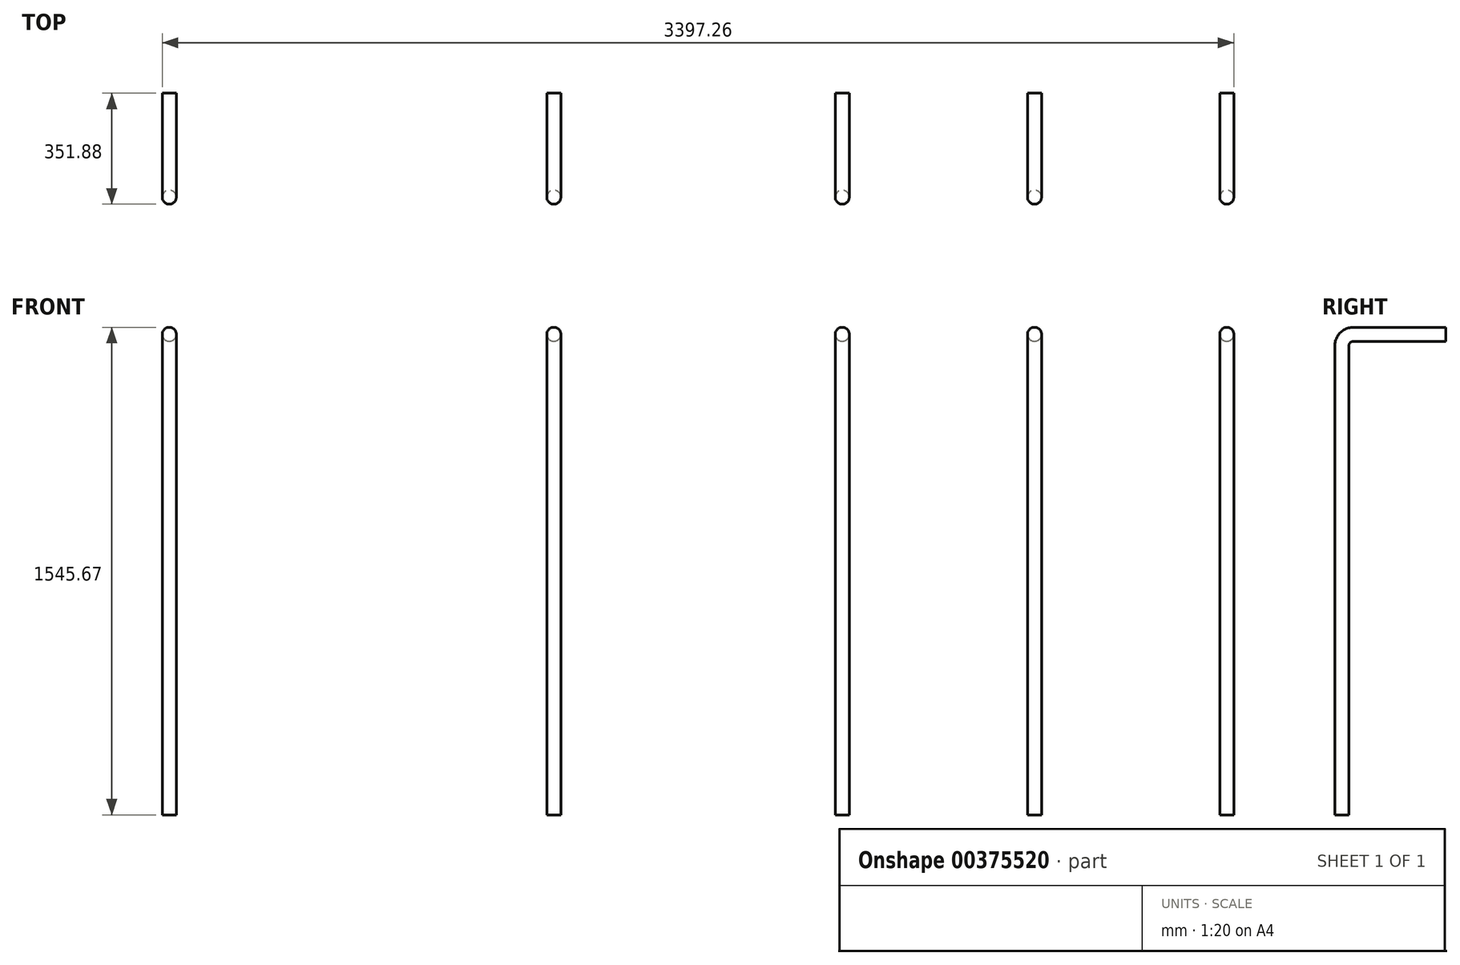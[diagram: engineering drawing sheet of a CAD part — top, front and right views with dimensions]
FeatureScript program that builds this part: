
annotation { "Feature Type Name" : "Feature", "Feature Type Description" : "" }
export const myFeature = defineFeature(function(context is Context, id is Id, definition is map)
    precondition{}
    {
        {
            var Q0;
            Q0=qCreatedBy(makeId("Top.planeOp"),FACE);
            cPlane(context, id + "F0", {"entities" : qUnion([Q0]), "cplaneType" : CPlaneType.OFFSET, "offset" : 381 * mm, "width" : 152.4 * mm, "height" : 152.4 * mm});
        }
        {
            var Q0;
            Q0=qCreatedBy(makeId("Top.planeOp"),FACE);
            cPlane(context, id + "F1", {"entities" : qUnion([Q0]), "cplaneType" : CPlaneType.OFFSET, "offset" : 685.8 * mm, "width" : 152.4 * mm, "height" : 152.4 * mm});
        }
        {
            var Q0;
            Q0=qCreatedBy(makeId("Top.planeOp"),FACE);
            cPlane(context, id + "F2", {"entities" : qUnion([Q0]), "cplaneType" : CPlaneType.OFFSET, "offset" : 1041.4 * mm, "width" : 152.4 * mm, "height" : 152.4 * mm});
        }
        {
            var Q0;
            Q0=qCreatedBy(makeId("Top.planeOp"),FACE);
            var sketch = newSketch(context, id + "F3", { "sketchPlane" : qUnion([Q0])});
            skLineSegment(sketch, "E0.bottom", {"start": v(-1727.2, 190.5) * mm, "end": v(1727.2, 190.5) * mm});
            skLineSegment(sketch, "E0.top", {"start": v(-1727.2, -190.5) * mm, "end": v(1727.2, -190.5) * mm});
            skLineSegment(sketch, "E0.left", {"start": v(-1727.2, 190.5) * mm, "end": v(-1727.2, -190.5) * mm});
            skLineSegment(sketch, "E0.right", {"start": v(1727.2, 190.5) * mm, "end": v(1727.2, -190.5) * mm});
            skPoint(sketch, "E0.middle", {"position": v(0, 0) * mm});
            skSolve(sketch);
        }
        {
            var Q0;
            Q0=qCreatedBy(id+"F1.planeOp",FACE);
            var sketch = newSketch(context, id + "F4", { "sketchPlane" : qUnion([Q0])});
            skLineSegment(sketch, "E1.0.0", {"start": v(-1727.2, 190.5) * mm, "end": v(-1727.2, -190.5) * mm});
            skLineSegment(sketch, "E1.0.1", {"start": v(-1727.2, -190.5) * mm, "end": v(1727.2, -190.5) * mm});
            skLineSegment(sketch, "E1.0.2", {"start": v(1727.2, -190.5) * mm, "end": v(1727.2, 190.5) * mm});
            skLineSegment(sketch, "E1.0.3", {"start": v(1727.2, 190.5) * mm, "end": v(-1727.2, 190.5) * mm});
            skSolve(sketch);
        }
        {
            var Q0;
            Q0=qCreatedBy(id+"F2.planeOp",FACE);
            var sketch = newSketch(context, id + "F5", { "sketchPlane" : qUnion([Q0])});
            skLineSegment(sketch, "E2.bottom", {"start": v(-406.4, -190.5) * mm, "end": v(-1727.2, -190.5) * mm});
            skLineSegment(sketch, "E2.top", {"start": v(-406.4, 190.5) * mm, "end": v(-1727.2, 190.5) * mm});
            skLineSegment(sketch, "E2.left", {"start": v(-406.4, -190.5) * mm, "end": v(-406.4, 190.5) * mm});
            skLineSegment(sketch, "E2.right", {"start": v(-1727.2, -190.5) * mm, "end": v(-1727.2, 190.5) * mm});
            skPoint(sketch, "E2.middle", {"position": v(-1066.8, 0) * mm});
            skLineSegment(sketch, "E3.bottom", {"start": v(1727.2, -190.5) * mm, "end": v(406.4, -190.5) * mm});
            skLineSegment(sketch, "E3.top", {"start": v(1727.2, 190.5) * mm, "end": v(406.4, 190.5) * mm});
            skLineSegment(sketch, "E3.left", {"start": v(1727.2, -190.5) * mm, "end": v(1727.2, 190.5) * mm});
            skLineSegment(sketch, "E3.right", {"start": v(406.4, -190.5) * mm, "end": v(406.4, 190.5) * mm});
            skPoint(sketch, "E3.middle", {"position": v(1066.8, 0) * mm});
            skSolve(sketch);
        }
        {
            var Q0;
            Q0=qCreatedBy(id+"F0.planeOp",FACE);
            var sketch = newSketch(context, id + "F6", { "sketchPlane" : qUnion([Q0])});
            skLineSegment(sketch, "E4.0.1", {"start": v(-406.4, 190.5) * mm, "end": v(-1727.2, 190.5) * mm});
            skLineSegment(sketch, "E4.0.2", {"start": v(-1727.2, 190.5) * mm, "end": v(-1727.2, -190.5) * mm});
            skLineSegment(sketch, "E4.0.3", {"start": v(-1727.2, -190.5) * mm, "end": v(-406.4, -190.5) * mm});
            skLineSegment(sketch, "E5.0.0", {"start": v(1727.2, -190.5) * mm, "end": v(1727.2, 190.5) * mm});
            skLineSegment(sketch, "E5.0.1", {"start": v(1727.2, 190.5) * mm, "end": v(406.4, 190.5) * mm});
            skLineSegment(sketch, "E5.0.2", {"start": v(406.4, 190.5) * mm, "end": v(406.4, -190.5) * mm});
            skLineSegment(sketch, "E5.0.3", {"start": v(406.4, -190.5) * mm, "end": v(1727.2, -190.5) * mm});
            skSolve(sketch);
        }
        {
            var Q0;
            Q0=qCreatedBy(makeId("Top.planeOp"),FACE);
            var sketch = newSketch(context, id + "F7", { "sketchPlane" : qUnion([Q0])});
            skCircle(sketch, "E6", {"center": v(-1676.4, -139.7) * mm, "radius": 22.23 * mm});
            skLineSegment(sketch, "E7", {"start": v(-1727.2, -139.7) * mm, "end": v(1727.2, -139.7) * mm, "construction": true});
            skLineSegment(sketch, "E8", {"start": v(-1676.4, -139.7) * mm, "end": v(-1676.4, -2659.55) * mm});
            skLineSegment(sketch, "E9", {"start": v(-457.2, -139.7) * mm, "end": v(-457.2, -2659.55) * mm});
            skLineSegment(sketch, "E10", {"start": v(457.2, -139.7) * mm, "end": v(457.2, -2659.55) * mm});
            skLineSegment(sketch, "E11", {"start": v(1066.8, -139.7) * mm, "end": v(1066.8, -2659.55) * mm});
            skLineSegment(sketch, "E12", {"start": v(1676.4, -139.7) * mm, "end": v(1676.4, -2659.55) * mm});
            skLineSegment(sketch, "E13", {"start": v(457.2, -139.7) * mm, "end": v(-457.2, -139.7) * mm, "construction": true});
            skPoint(sketch, "E14", {"position": v(0, -139.7) * mm});
            skCircle(sketch, "E15", {"center": v(-457.2, -139.7) * mm, "radius": 22.23 * mm});
            skCircle(sketch, "E16", {"center": v(457.2, -139.7) * mm, "radius": 22.23 * mm});
            skCircle(sketch, "E17", {"center": v(1066.8, -139.7) * mm, "radius": 22.23 * mm});
            skCircle(sketch, "E18", {"center": v(1676.4, -139.7) * mm, "radius": 22.23 * mm});
            skSolve(sketch);
        }
        {
            var Q0;
            Q0=qCreatedBy(makeId("Top.planeOp"),FACE);
            var sketch = newSketch(context, id + "F8", { "sketchPlane" : qUnion([Q0])});
            skSolve(sketch);
        }
        {
            var Q0;
            Q0=qCreatedBy(makeId("Right.planeOp"),FACE);
            var sketch = newSketch(context, id + "F9", { "sketchPlane" : qUnion([Q0])});
            skLineSegment(sketch, "E19", {"start": v(-140.25, 0) * mm, "end": v(-140.25, 1485.9) * mm});
            skLineSegment(sketch, "E20", {"start": v(-102.15, 1524) * mm, "end": v(189.95, 1524) * mm});
            skPoint(sketch, "E21.visualSharp", {"position": v(-140.25, 1524) * mm});
            skArc(sketch, "E21.filletArc", {"start": v(-102.15, 1524) * mm, "mid": v(-129.1, 1512.84) * mm, "end": v(-140.25, 1485.9) * mm});
            skSolve(sketch);
        }
        {
            var Q0;
            Q0=qCreatedBy(makeId("Right.planeOp"),FACE);
            var Q1;
            Q1=sQuery(id+"F7.wireOp",VERTEX,"E16.center");
            cPlane(context, id + "F10", {"entities" : qUnion([Q0, Q1]), "cplaneType" : CPlaneType.PLANE_POINT, "offset" : 25.4 * mm, "width" : 152.4 * mm, "height" : 152.4 * mm});
        }
        {
            var Q0;
            Q0=qCreatedBy(id+"F10.planeOp",FACE);
            var sketch = newSketch(context, id + "F11", { "sketchPlane" : qUnion([Q0])});
            skLineSegment(sketch, "E22.0", {"start": v(-140.25, 0) * mm, "end": v(-140.25, 1485.9) * mm});
            skArc(sketch, "E23.0", {"start": v(-102.15, 1524) * mm, "mid": v(-129.1, 1512.84) * mm, "end": v(-140.25, 1485.9) * mm});
            skLineSegment(sketch, "E24.0", {"start": v(-102.15, 1524) * mm, "end": v(189.95, 1524) * mm});
            skSolve(sketch);
        }
        {
            var Q0;
            Q0=qCreatedBy(makeId("Right.planeOp"),FACE);
            var Q1;
            Q1=sQuery(id+"F7.wireOp",VERTEX,"E15.center");
            cPlane(context, id + "F12", {"entities" : qUnion([Q0, Q1]), "cplaneType" : CPlaneType.PLANE_POINT, "offset" : 25.4 * mm, "width" : 152.4 * mm, "height" : 152.4 * mm});
        }
        {
            var Q0;
            Q0=qCreatedBy(makeId("Right.planeOp"),FACE);
            var Q1;
            Q1=sQuery(id+"F7.wireOp",VERTEX,"E17.center");
            cPlane(context, id + "F13", {"entities" : qUnion([Q0, Q1]), "cplaneType" : CPlaneType.PLANE_POINT, "offset" : 25.4 * mm, "width" : 152.4 * mm, "height" : 152.4 * mm});
        }
        {
            var Q0;
            Q0=qCreatedBy(makeId("Right.planeOp"),FACE);
            var Q1;
            Q1=sQuery(id+"F7.wireOp",VERTEX,"E18.center");
            cPlane(context, id + "F14", {"entities" : qUnion([Q0, Q1]), "cplaneType" : CPlaneType.PLANE_POINT, "offset" : 25.4 * mm, "width" : 152.4 * mm, "height" : 152.4 * mm});
        }
        {
            var Q0;
            Q0=qCreatedBy(makeId("Right.planeOp"),FACE);
            var Q1;
            Q1=sQuery(id+"F7.wireOp",VERTEX,"E8.end");
            cPlane(context, id + "F15", {"entities" : qUnion([Q0, Q1]), "cplaneType" : CPlaneType.PLANE_POINT, "offset" : 25.4 * mm, "width" : 152.4 * mm, "height" : 152.4 * mm});
        }
        {
            var Q0;
            Q0=qCreatedBy(id+"F12.planeOp",FACE);
            var sketch = newSketch(context, id + "F16", { "sketchPlane" : qUnion([Q0])});
            skLineSegment(sketch, "E25.0", {"start": v(-102.15, 1524) * mm, "end": v(189.95, 1524) * mm});
            skLineSegment(sketch, "E26.0", {"start": v(-140.25, 0) * mm, "end": v(-140.25, 1485.9) * mm});
            skPoint(sketch, "E27.0", {"position": v(-129.1, 1512.84) * mm});
            skArc(sketch, "E28.0", {"start": v(-102.15, 1524) * mm, "mid": v(-129.1, 1512.84) * mm, "end": v(-140.25, 1485.9) * mm});
            skSolve(sketch);
        }
        {
            var Q0;
            Q0=qCreatedBy(id+"F13.planeOp",FACE);
            var sketch = newSketch(context, id + "F17", { "sketchPlane" : qUnion([Q0])});
            skLineSegment(sketch, "E29.0", {"start": v(-102.15, 1524) * mm, "end": v(189.95, 1524) * mm});
            skArc(sketch, "E30.0", {"start": v(-102.15, 1524) * mm, "mid": v(-129.1, 1512.84) * mm, "end": v(-140.25, 1485.9) * mm});
            skLineSegment(sketch, "E31.0", {"start": v(-140.25, 0) * mm, "end": v(-140.25, 1485.9) * mm});
            skSolve(sketch);
        }
        {
            var Q0;
            Q0=qCreatedBy(id+"F15.planeOp",FACE);
            var sketch = newSketch(context, id + "F18", { "sketchPlane" : qUnion([Q0])});
            skLineSegment(sketch, "E32.0", {"start": v(-102.15, 1524) * mm, "end": v(189.95, 1524) * mm});
            skArc(sketch, "E33.0", {"start": v(-102.15, 1524) * mm, "mid": v(-129.1, 1512.84) * mm, "end": v(-140.25, 1485.9) * mm});
            skLineSegment(sketch, "E34.0", {"start": v(-140.25, 0) * mm, "end": v(-140.25, 1485.9) * mm});
            skSolve(sketch);
        }
        {
            var Q0;
            Q0=makeQuery(id+"F7.imprint","IMPRINT",FACE,{"disambiguationData":[TD([[makeQuery(id+"F7.imprint","IMPRINT",EDGE,{"derivedFrom":sQuery(id+"F7.wireOp",EDGE,"E18")}),1.0]])]});
            var Q1;
            Q1=makeQuery(id+"F7.imprint","IMPRINT",FACE,{"disambiguationData":[TD([[makeQuery(id+"F7.imprint","IMPRINT",EDGE,{"derivedFrom":sQuery(id+"F7.wireOp",EDGE,"E17")}),1.0]])]});
            var Q2;
            Q2=makeQuery(id+"F7.imprint","IMPRINT",FACE,{"disambiguationData":[TD([[makeQuery(id+"F7.imprint","IMPRINT",EDGE,{"derivedFrom":sQuery(id+"F7.wireOp",EDGE,"E16")}),1.0]])]});
            var Q3;
            Q3=makeQuery(id+"F7.imprint","IMPRINT",FACE,{"disambiguationData":[TD([[makeQuery(id+"F7.imprint","IMPRINT",EDGE,{"derivedFrom":sQuery(id+"F7.wireOp",EDGE,"E15")}),1.0]])]});
            var Q4;
            Q4=makeQuery(id+"F7.imprint","IMPRINT",FACE,{"disambiguationData":[TD([[makeQuery(id+"F7.imprint","IMPRINT",EDGE,{"derivedFrom":sQuery(id+"F7.wireOp",EDGE,"E6")}),1.0]])]});
            var Q5;
            Q5=sQuery(id+"F18.wireOp",EDGE,"E34.0");
            var Q6;
            Q6=sQuery(id+"F18.wireOp",EDGE,"E33.0");
            var Q7;
            Q7=sQuery(id+"F18.wireOp",EDGE,"E32.0");
            sweep(context, id + "F19", {"profiles" : qUnion([Q0, Q1, Q2, Q3, Q4]), "path" : qUnion([Q5, Q6, Q7])});
        }
    });
